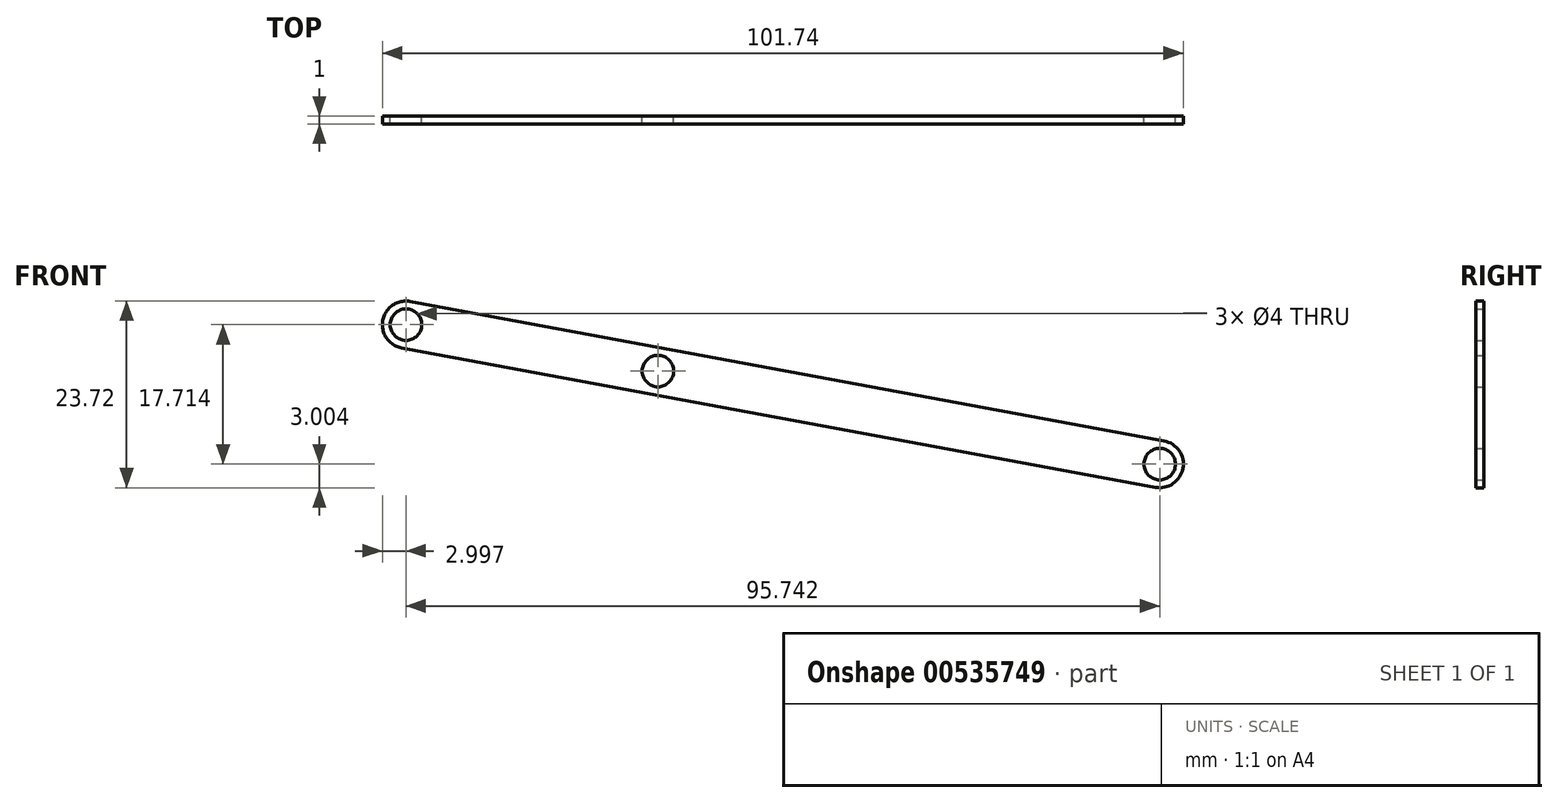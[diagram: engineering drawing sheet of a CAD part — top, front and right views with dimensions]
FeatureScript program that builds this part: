
annotation { "Feature Type Name" : "Feature", "Feature Type Description" : "" }
export const myFeature = defineFeature(function(context is Context, id is Id, definition is map)
    precondition{}
    {
        {
            var Q0;
            Q0=qCreatedBy(makeId("Front.planeOp"),FACE);
            var sketch = newSketch(context, id + "F0", { "sketchPlane" : qUnion([Q0])});
            skArc(sketch, "E0", {"start": v(-57.48, 30.53) * mm, "mid": v(-60.97, 28.12) * mm, "end": v(-58.57, 24.63) * mm});
            skArc(sketch, "E1", {"start": v(37.17, 6.91) * mm, "mid": v(40.67, 9.32) * mm, "end": v(38.27, 12.81) * mm});
            skLineSegment(sketch, "E2", {"start": v(-57.48, 30.53) * mm, "end": v(38.27, 12.81) * mm});
            skLineSegment(sketch, "E3", {"start": v(37.17, 6.91) * mm, "end": v(-58.57, 24.63) * mm});
            skCircle(sketch, "E4", {"center": v(-58.02, 27.58) * mm, "radius": 2 * mm});
            skCircle(sketch, "E5", {"center": v(37.72, 9.86) * mm, "radius": 2 * mm});
            skCircle(sketch, "E6", {"center": v(-26.02, 21.68) * mm, "radius": 2 * mm});
            skSolve(sketch);
        }
        {
            var Q0;
            Q0 = qSketchRegion(id + "F0", true);
            extrude(context, id + "F1", {"entities" : qUnion([Q0]), "endBound" : BoundingType.SYMMETRIC, "depth" : 1 * mm, "offsetDistance" : 25 * mm});
        }
    });
